# Revit family: DLB060013-FR
name_source: partatom
category: Appareils sanitaires
revit_build: Autodesk Revit 2015 (Build: 20140606_1530(x64)
units: mm (PartAtom-declared; Revit-internal decimal feet)

## types (1)
- Type 1
    Commentaires du type = WC
    Descriptif = WC suspendu. 
Compatible avec tous les bâti-supports standards du marché. 
Design pur et élégant. 
Inox 304 bactériostatique. 
Épaisseur Inox : 1,5 mm. 
Cuvette emboutie, sans soudures, pour un entretien facile et une meilleure hygiène. 
Intérieur de la cuvette poli et bords arrondis pour un nettoyage aisé. 
Rebord à effet d’eau intégré. 
Arrivée d’eau horizontale Ø 55 mm. 
Évacuation d’eau horizontale Ø 100 mm. 
Économie d’eau : fonctionne avec 4 L d'eau et plus. 
Dessous fermé. 
Perçages pour la fixation de l’abattant. Livré avec cache-trous en Inox pour utilisation sans abattant. 
Installation rapide et facile : montage par l’avant grâce à une platine de fixation en Inox. 
Livré avec platine de montage et 6 vis antivol TORX. 
Marquage CE. Conforme à la norme EN 997 pour une chasse d’eau 4 L.
Poids : 11 kg.
    Description = DELABIE, fabricant français, est le leader européen de l'équipement sanitaire pour les établissements recevant du public. Robinetteries, solutions pour personnes à mobilité réduite, appareils sanitaires, destinés aux écoles, lieux de loisirs, bureaux, hôpitaux, aéroports, ...
    Fabricant = DELABIE
    Famille de produits = WC
    Finition = Inox 304 poli satiné
    Hauteur = 350 mm  [stored 1.14829 ft]
    Largeur = 360 mm  [stored 1.1811 ft]
    Lien CCTP = http://www.delabie.fr
    Lien certification = http://www.delabie.fr
    Lien fiche produit = http://www.delabie.fr
    Lien notice d'installation = http://www.delabie.fr
    Modèle = S21 S
    Profondeur = 535 mm  [stored 1.75525 ft]
    Radius (Entrée) = 45 mm  [stored 0.147638 ft]
    Radius (Sortie) = 100 mm  [stored 0.328084 ft]
    Référence = 110310
    URL = http://www.delabie.fr

note: [stored X ft] marks values corroborated as IEEE doubles in the binary element streams (Revit-internal decimal feet)

## geometry (parser evidence)
native form markers: Blend x16, Sweep x12
no freeform markers — native parametric forms only
